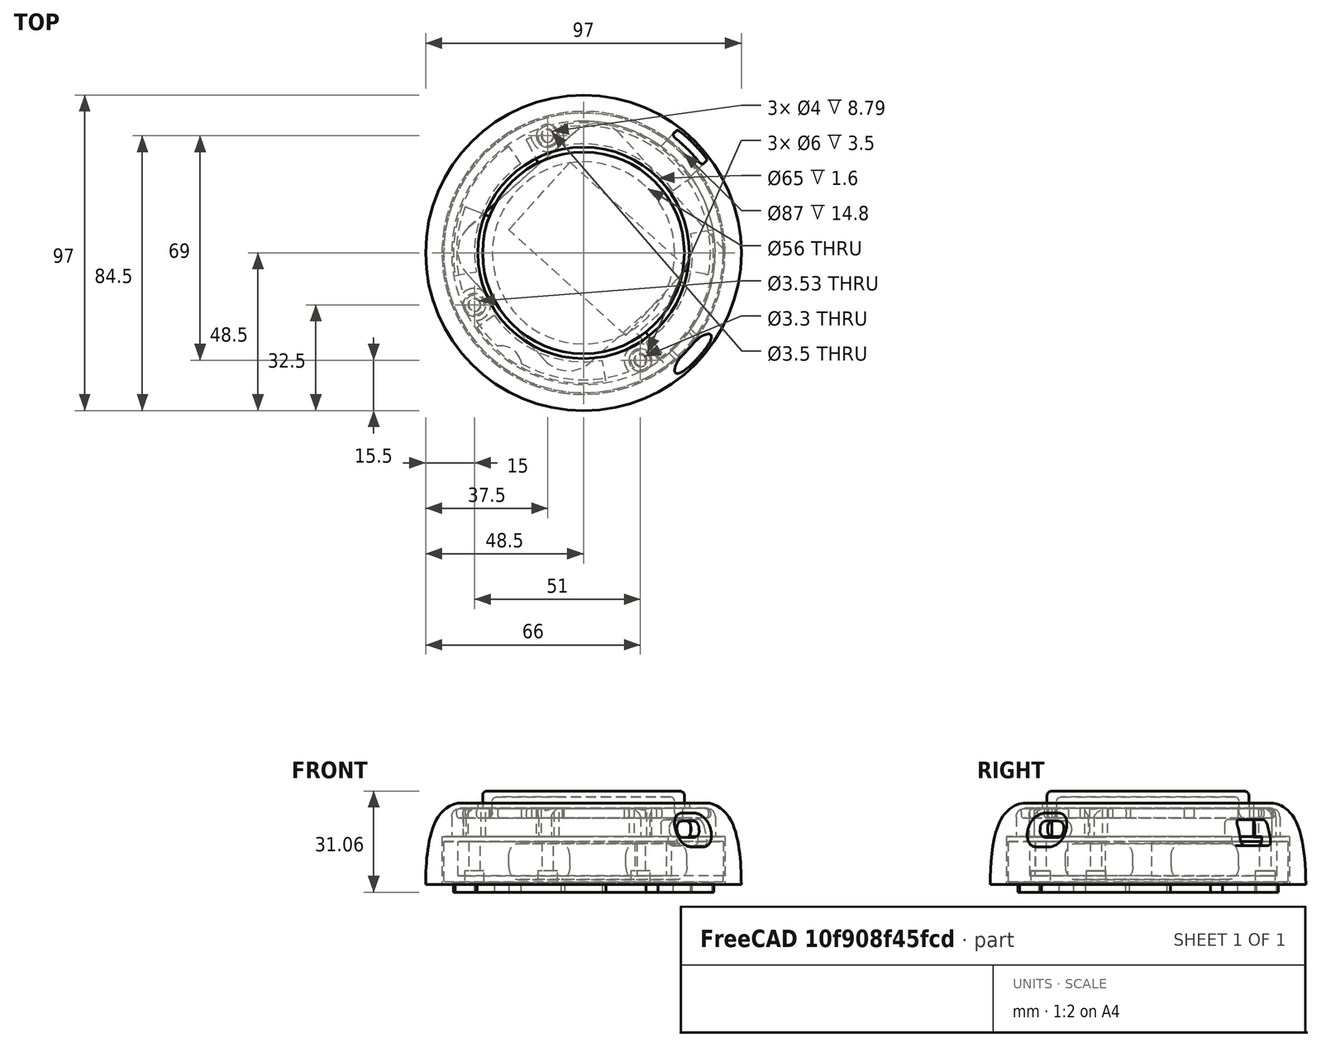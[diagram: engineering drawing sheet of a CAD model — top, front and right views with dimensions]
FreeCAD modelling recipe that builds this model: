
FCSTD DOCUMENT  (FreeCAD 1.0R39109 (Git))
Label: slimCasing_new
License: All rights reserved
LicenseURL: https://en.wikipedia.org/wiki/All_rights_reserved
objects: Sketcher::SketchObject×11, PartDesign::Body×5, PartDesign::Pocket×5, PartDesign::Pad×4, PartDesign::Revolution×2, PartDesign::Plane×2, Mesh::Feature×1, PartDesign::Fillet×1, PartDesign::Chamfer×1, PartDesign::PolarPattern×1
note: 70 computed .brp shape members not serialized (recipe doc carries the construction recipe); baked Part::Feature solids carry a one-line shape summary decoded from their .brp

FEATURE [Sketcher::SketchObject] Sketch
  ArcFitTolerance = 1e-06
  AttachmentSupport = -> [XZ_Plane]
  FullyConstrained = true
  MakeInternals = false
  MapMode = 5
  Placement = pos=(0,0,0) rot=(1,0,0;1.5708rad)
  sketch-geometry (17):
    g0: LineSegment StartX=-31 StartY=12 StartZ=0 EndX=-31 EndY=8 EndZ=0
    g1: LineSegment StartX=-31 StartY=8 StartZ=0 EndX=-38 EndY=8 EndZ=0
    g2: LineSegment StartX=-39 StartY=7 StartZ=0 EndX=-39 EndY=6 EndZ=0
    g3: LineSegment StartX=-38 StartY=5 StartZ=0 EndX=-29.8 EndY=5 EndZ=0
    g4: LineSegment StartX=-28 StartY=6.8 StartZ=0 EndX=-28 EndY=10.2 EndZ=0
    g5: LineSegment StartX=-26.7 StartY=11.5 StartZ=0 EndX=0 EndY=11.5 EndZ=0
    g6: LineSegment StartX=0 StartY=11.5 StartZ=0 EndX=0 EndY=13.3 EndZ=0
    g7: ArcOfCircle CenterX=-29.7 CenterY=12 CenterZ=0 NormalX=0 NormalY=0 NormalZ=1 AngleXU=0 Radius=1.3 StartAngle=1.5708 EndAngle=3.14159
    g8: ArcOfCircle CenterX=-26.7 CenterY=10.2 CenterZ=0 NormalX=0 NormalY=0 NormalZ=1 AngleXU=0 Radius=1.3 StartAngle=1.5708 EndAngle=3.14159
    g9: GeomPoint [constr] X=-28 Y=11.5 Z=0
    g10: GeomPoint [constr] X=-31 Y=8 Z=0
    g11: ArcOfCircle CenterX=-29.8 CenterY=6.8 CenterZ=0 NormalX=0 NormalY=0 NormalZ=1 AngleXU=0 Radius=1.8 StartAngle=4.71239 EndAngle=6.28319
    g12: GeomPoint [constr] X=-28 Y=5 Z=0
    g13: ArcOfCircle CenterX=-38 CenterY=7 CenterZ=0 NormalX=0 NormalY=0 NormalZ=1 AngleXU=0 Radius=1 StartAngle=1.5708 EndAngle=3.14159
    g14: GeomPoint [constr] X=-39 Y=8 Z=0
    g15: ArcOfCircle CenterX=-38 CenterY=6 CenterZ=0 NormalX=0 NormalY=0 NormalZ=1 AngleXU=0 Radius=1 StartAngle=3.14159 EndAngle=4.71239
    g16: LineSegment StartX=-29.7 StartY=13.3 StartZ=0 EndX=0 EndY=13.3 EndZ=0
  constraints (42):
    c: Vertical(g0)
    c: Horizontal(g1)
    c: Vertical(g2)
    c: Horizontal(g3)
    c: Vertical(g4)
    c: Horizontal(g5)
    c: Coincident(g5,g6)
    c: Vertical(g6)
    c: DistanceY(g10,g9) = 3.5
    c: DistanceX(g10,g9) = 3
    c: DistanceY(g-1,g5) = 11.5
    c: Tangent(g0,g7) = -1.5708
    c: PointOnObject(g9,g4)
    c: PointOnObject(g9,g5)
    c: Tangent(g4,g8) = 1.5708
    c: Tangent(g5,g8) = 1.5708
    c: PointOnObject(g12,g3)
    c: PointOnObject(g12,g4)
    c: Tangent(g3,g11) = -1.5708
    c: Tangent(g4,g11) = -1.5708
    c: PointOnObject(g14,g2)
    c: PointOnObject(g14,g1)
    c: Tangent(g2,g13) = -1.5708
    c: Tangent(g1,g13) = -1.5708
    c: Tangent(g2,g15) = -1.5708
    c: Tangent(g3,g15) = -1.5708
    c: Equal(g7,g8)
    c: Coincident(g1,g10)
    c: Coincident(g0,g1)
    c: DistanceY(g0,g0) = 4
    c: Radius(g11) = 1.8
    c: Equal(g13,g15)
    c: Radius(g13) = 1
    c: PointOnObject(g5,g-2)
    c: DistanceY(g3,g1) = 3
    c: DistanceY(g7,g7) = 1.3
    c: Horizontal(g16)
    c: Coincident(g6,g16)
    c: Tangent(g7,g16) = 1.5708
    c: Distance(g0,g-2) = 31
    c: Distance(g9,g16) = 1.8
    c: Distance(g2,g-2) = 39
FEATURE [Mesh::Feature] PCB_Board  label="PCB Board"
  Placement = pos=(-64.6,63.9,0.05) rot=(0,0,1;0rad)
FEATURE [PartDesign::Revolution] Revolution
  Angle = 360
  Angle2 = 60
  Axis = (0,2e-16,1)
  Base = (0,0,0)
  Placement = pos=(0,0,0) rot=(1,0,0;1.5708rad)
  Profile = -> Sketch
  ReferenceAxis = -> Sketch [V_Axis]
  Refine = true
  Suppressed = false
  Type = 0
FEATURE [Sketcher::SketchObject] Sketch001
  ArcFitTolerance = 1e-06
  AttachmentSupport = -> [Revolution]
  FullyConstrained = false
  MakeInternals = false
  MapMode = 5
  Placement = pos=(0,2.2e-15,5) rot=(1,0,0;3.14159rad)
  sketch-geometry (17):
    g0: ArcOfCircle CenterX=25.2748 CenterY=34.7877 CenterZ=0 NormalX=0 NormalY=0 NormalZ=1 AngleXU=0 Radius=6.2 StartAngle=2.58543 EndAngle=5.58271
    g1: ArcOfCircle CenterX=0 CenterY=0 CenterZ=0 NormalX=0 NormalY=0 NormalZ=1 AngleXU=0 Radius=43 StartAngle=0.798167 EndAngle=1.08679
    g2: LineSegment [constr] StartX=25.2748 StartY=34.7877 StartZ=0 EndX=0 EndY=0 EndZ=0
    g3: ArcOfCircle CenterX=0 CenterY=0 CenterZ=0 NormalX=0 NormalY=0 NormalZ=1 AngleXU=0 Radius=43 StartAngle=2.2555 EndAngle=2.98853
    g4: LineSegment [constr] StartX=0 StartY=0 StartZ=0 EndX=-42.4024 EndY=26.496 EndZ=0
    g5: LineSegment [constr] StartX=0 StartY=0 StartZ=0 EndX=32.3963 EndY=-28.2751 EndZ=0
    g6: LineSegment StartX=40.3774 StartY=-14.7873 StartZ=0 EndX=29.1093 EndY=-10.6606 EndZ=0
    g7: LineSegment StartX=20.1117 StartY=-38.0069 StartZ=0 EndX=14.4991 EndY=-27.4003 EndZ=0
    g8: ArcOfCircle CenterX=0 CenterY=0 CenterZ=0 NormalX=0 NormalY=0 NormalZ=1 AngleXU=0 Radius=31 StartAngle=5.19909 EndAngle=5.93213
    g9: ArcOfCircle CenterX=0 CenterY=0 CenterZ=0 NormalX=0 NormalY=0 NormalZ=1 AngleXU=0 Radius=43 StartAngle=5.19909 EndAngle=5.93213
    g10: LineSegment [constr] StartX=14.4991 StartY=-27.4003 StartZ=0 EndX=29.1093 EndY=-10.6606 EndZ=0
    g11: Circle CenterX=-37.7489 CenterY=-0.6901 CenterZ=0 NormalX=0 NormalY=0 NormalZ=1 AngleXU=0 Radius=5
    g12: Circle CenterX=4.78434 CenterY=36.8193 CenterZ=0 NormalX=0 NormalY=0 NormalZ=1 AngleXU=0 Radius=5
    g13: Circle CenterX=36.7704 CenterY=-6.49344 CenterZ=0 NormalX=0 NormalY=0 NormalZ=1 AngleXU=0 Radius=5
    g14: ArcOfCircle CenterX=0 CenterY=0 CenterZ=0 NormalX=0 NormalY=0 NormalZ=1 AngleXU=0 Radius=31 StartAngle=2.2555 EndAngle=2.98853
    g15: LineSegment StartX=-19.6056 StartY=24.0129 StartZ=0 EndX=-27.1949 EndY=33.3082 EndZ=0
    g16: LineSegment StartX=-42.4973 StartY=6.55585 StartZ=0 EndX=-30.6376 EndY=4.72631 EndZ=0
  constraints (48):
    c: Coincident(g1,g0)
    c: Coincident(g1,g0)
    c: Coincident(g2,g0)
    c: Angle(g-1,g2) = 0.942478
    c: Distance(g4,g4) = 50
    c: Angle(g4,g-1) = 0.558505
    c: Coincident(g8,g6)
    c: Coincident(g8,g7)
    c: Distance(g6,g6) = 12
    c: Coincident(g9,g6)
    c: Coincident(g9,g7)
    c: Coincident(g10,g7)
    c: Coincident(g10,g6)
    c: Perpendicular(g5,g10)
    c: Equal(g13,g12)
    c: Equal(g11,g12)
    c: Diameter(g12) = 10
    c: DistanceX(g11,g1) = 37.7489
    c: DistanceY(g11,g1) = 0.6901
    c: DistanceX(g13) = 36.7704
    c: DistanceY(g13) = -6.49344
    c: DistanceX(g12) = 4.78434
    c: DistanceY(g12) = 36.8193
    c: Coincident(g1,g2)
    c: Coincident(g1,g3)
    c: Coincident(g1,g4)
    c: Coincident(g1,g5)
    c: Coincident(g1,g8)
    c: Coincident(g1,g9)
    c: Coincident(g1,g-1)
    c: Radius(g0) = 6.2
    c: Distance(g0,g1) = 43
    c: PointOnObject(g0,g1)
    c: Radius(g3) = 43
    c: Radius(g9) = 43
    c: Angle(g7,g6) = 0.733038
    c: PointOnObject(g5,g9)
    c: Coincident(g14,g1)
    c: Equal(g8,g14)
    c: Coincident(g15,g14)
    c: Coincident(g15,g3)
    c: Coincident(g16,g3)
    c: Coincident(g16,g14)
    c: Perpendicular(g14,g16)
    c: Perpendicular(g14,g15)
    c: Angle(g15,g16) = 0.733038
    c: Distance(g16,g16) = 12
    c: Perpendicular(g9,g7)
FEATURE [Sketcher::SketchObject] Sketch027
  ArcFitTolerance = 0
  FullyConstrained = true
  MakeInternals = false
  MapMode = 5
  sketch-geometry (4):
    g0: LineSegment StartX=-24.25 StartY=14 StartZ=0 EndX=24.25 EndY=14 EndZ=0
    g1: LineSegment StartX=24.25 StartY=14 StartZ=0 EndX=24.25 EndY=-14 EndZ=0
    g2: LineSegment StartX=24.25 StartY=-14 StartZ=0 EndX=-24.25 EndY=-14 EndZ=0
    g3: LineSegment StartX=-24.25 StartY=-14 StartZ=0 EndX=-24.25 EndY=14 EndZ=0
  constraints (11):
    c: Coincident(g0,g1)
    c: Coincident(g1,g2)
    c: Coincident(g2,g3)
    c: Coincident(g3,g0)
    c: Horizontal(g0)
    c: Horizontal(g2)
    c: Vertical(g1)
    c: Vertical(g3)
    c: Symmetric(g0,g1,g-1)
    c: DistanceX(g0,g0) = 48.5
    c: DistanceY(g1,g1) = 28
FEATURE [PartDesign::Pad] Pad004
  Direction = (0,0,1)
  Length = 11
  Length2 = 10
  Profile = -> Sketch027
  ReferenceAxis = -> Sketch027 [N_Axis]
  Suppressed = false
  Type = 0
FEATURE [PartDesign::Fillet] Fillet002
  Base = -> Pad004 [Edge4,Edge3,Edge10,Edge9]
  BaseFeature = -> Pad004
  Radius = 4
  SupportTransform = false
  Suppressed = false
  UseAllEdges = false
FEATURE [PartDesign::Body] Body005  label="Batterie"
  AllowCompound = false
  Group = -> [Sketch027,Pad004,Fillet002]
  Placement = pos=(4.42123,1.23614,-11.6) rot=(0,0,1;5.5484rad)
  Tip = -> Fillet002
FEATURE [PartDesign::Pocket] Pocket
  BaseFeature = -> Revolution
  Direction = (0,0,1)
  Length = 5
  Length2 = 5
  Placement = pos=(0,0,0) rot=(1,0,0;1.5708rad)
  Profile = -> Sketch001
  ReferenceAxis = -> Sketch001 [N_Axis]
  Refine = true
  Suppressed = false
  Type = 0
FEATURE [PartDesign::Body] Body  label="Buzzerkopf"
  AllowCompound = false
  Group = -> [Sketch,Revolution,Sketch001,Pocket]
  Origin = -> Origin
  Placement = pos=(0,0,2.23) rot=(0,0,1;5.02655rad)
  Tip = -> Pocket
FEATURE [Sketcher::SketchObject] Sketch028
  ArcFitTolerance = 1e-06
  AttachmentSupport = -> [YZ_Plane001]
  FullyConstrained = false
  MakeInternals = false
  MapMode = 5
  Placement = pos=(0,0,0) rot=(0.57735,0.57735,0.57735;2.0944rad)
  sketch-geometry (16):
    g0: LineSegment StartX=32.5 StartY=10.29 StartZ=0 EndX=37.81 EndY=10.29 EndZ=0
    g1: LineSegment StartX=40.5 StartY=7.6 StartZ=0 EndX=40.5 EndY=1.6 EndZ=0
    g2: LineSegment StartX=40.5 StartY=1.6 StartZ=0 EndX=43.5 EndY=1.6 EndZ=0
    g3: LineSegment StartX=43.5 StartY=1.6 StartZ=0 EndX=43.5 EndY=-13.2 EndZ=0
    g4: LineSegment StartX=43.5 StartY=-13.2 StartZ=0 EndX=48.5 EndY=-13.2 EndZ=0
    g5-g8: Circle [constr] x4 (B-spline internal-alignment scaffolding for g9; pole/knot coordinates omitted)
    g9: BSplineCurve PolesCount=5 KnotsCount=3 Degree=3 IsPeriodic=0
    g10: GeomPoint [constr] X=37.5 Y=11.89 Z=0
    g11: GeomPoint [constr] X=48.5 Y=-13.2 Z=0
    g12: ArcOfCircle CenterX=37.81 CenterY=7.6 CenterZ=0 NormalX=0 NormalY=0 NormalZ=1 AngleXU=0 Radius=2.69 StartAngle=0 EndAngle=1.5708
    g13: GeomPoint [constr] X=40.5 Y=10.29 Z=0
    g14: LineSegment StartX=37.5 StartY=11.89 StartZ=0 EndX=32.5 EndY=11.89 EndZ=0
    g15: LineSegment StartX=32.5 StartY=11.89 StartZ=0 EndX=32.5 EndY=10.29 EndZ=0
  constraints (41):
    c: Horizontal(g0)
    c: Coincident(g1,g2)
    c: Horizontal(g2)
    c: Coincident(g2,g3)
    c: Vertical(g3)
    c: Coincident(g3,g4)
    c: Horizontal(g4)
    c: InternalAlignment(g5-g8 -> g9) x4
    c: InternalAlignment(g10,g9)
    c: InternalAlignment(g11,g9)
    c: Coincident(g8,g4)
    c: Vertical(g1)
    c: DistanceX(g4,g4) = 5
    c: Distance(g2,g2) = 3
    c: Distance(g0,g-2) = 32.5
    c: Horizontal(g5,g9)
    c: Vertical(g7,g9)
    c: PointOnObject(g13,g0)
    c: PointOnObject(g13,g1)
    c: Tangent(g0,g12) = 1.5708
    c: Tangent(g1,g12) = 1.5708
    c: DistanceY(g1,g1) = 6
    c: Radius(g12) = 2.69
    c: DistanceY(g3,g3) = 14.8
    c: DistanceX(g5,g6) = 8
    c: DistanceY(g6,g5) = 1.8
    c: DistanceY(g9,g7) = 6.93
    c: Distance(g2,g-1) = 1.6
    c: Distance(g5,g-2) = 39
    c: Distance(g13,g-2) = 40.5
    c: Coincident(g14,g9)
    c: Horizontal(g14)
    c: Coincident(g15,g14)
    c: Coincident(g15,g0)
    c: Vertical(g15)
    c: DistanceY(g15,g15) = 1.6
    c: DistanceX(g14,g14) = 5
    c: Weight(g5) = 2.75
    c: Weight(g6) = 2.71
    c: Weight(g7) = 2.65
    c: Weight(g8) = 2.04
FEATURE [PartDesign::Revolution] Revolution001
  Angle = 360
  Angle2 = 60
  Axis = (0,0,1)
  Base = (0,0,0)
  Placement = pos=(0,0,0) rot=(1,1,1;2.0944rad)
  Profile = -> Sketch028
  ReferenceAxis = -> Sketch028 [V_Axis]
  Refine = true
  Reversed = true
  Suppressed = false
  Type = 0
FEATURE [Sketcher::SketchObject] Sketch029
  ArcFitTolerance = 1e-06
  AttachmentOffset = pos=(0,0,1.5) rot=(0,0,1;0rad)
  AttachmentSupport = -> [XY_Plane001]
  FullyConstrained = true
  MakeInternals = false
  MapMode = 5
  Placement = pos=(0,0,1.5) rot=(0,0,1;0rad)
  sketch-geometry (6):
    g0: Circle CenterX=-11 CenterY=36 CenterZ=0 NormalX=0 NormalY=0 NormalZ=1 AngleXU=0 Radius=3.5
    g1: Circle CenterX=17.5 CenterY=-33 CenterZ=0 NormalX=0 NormalY=0 NormalZ=1 AngleXU=0 Radius=3.5
    g2: Circle CenterX=-33.5 CenterY=-16 CenterZ=0 NormalX=0 NormalY=0 NormalZ=1 AngleXU=0 Radius=3.5
    g3: Circle CenterX=-11 CenterY=36 CenterZ=0 NormalX=0 NormalY=0 NormalZ=1 AngleXU=0 Radius=2
    g4: Circle CenterX=-33.5 CenterY=-16 CenterZ=0 NormalX=0 NormalY=0 NormalZ=1 AngleXU=0 Radius=2
    g5: Circle CenterX=17.5 CenterY=-33 CenterZ=0 NormalX=0 NormalY=0 NormalZ=1 AngleXU=0 Radius=2
  constraints (15):
    c: DistanceX(g0) = -11
    c: DistanceY(g0) = 36
    c: DistanceX(g2) = -33.5
    c: DistanceY(g2) = -16
    c: DistanceX(g1) = 17.5
    c: DistanceY(g1) = -33
    c: Equal(g1,g2)
    c: Equal(g2,g0)
    c: Diameter(g0) = 7
    c: Coincident(g3,g0)
    c: Coincident(g4,g2)
    c: Coincident(g5,g1)
    c: Equal(g5,g4)
    c: Equal(g4,g3)
    c: Diameter(g3) = 4
FEATURE [PartDesign::Pad] Pad
  BaseFeature = -> Revolution001
  Direction = (0,0,1)
  Length = 9
  Length2 = 10
  Placement = pos=(0,0,0) rot=(1,1,1;2.0944rad)
  Profile = -> Sketch029
  ReferenceAxis = -> Sketch029 [N_Axis]
  Refine = true
  Suppressed = false
  Type = 0
FEATURE [Sketcher::SketchObject] Sketch030
  ArcFitTolerance = 1e-06
  AttachmentSupport = -> [XY_Plane002]
  FullyConstrained = true
  MakeInternals = false
  MapMode = 5
  sketch-geometry (4):
    g0: Circle CenterX=0 CenterY=0 CenterZ=0 NormalX=0 NormalY=0 NormalZ=1 AngleXU=0 Radius=43
    g1: Circle CenterX=-33.5 CenterY=-16 CenterZ=0 NormalX=0 NormalY=0 NormalZ=1 AngleXU=0 Radius=1.765
    g2: Circle CenterX=17.5 CenterY=-33 CenterZ=0 NormalX=0 NormalY=0 NormalZ=1 AngleXU=0 Radius=1.65
    g3: Circle CenterX=-11 CenterY=36 CenterZ=0 NormalX=0 NormalY=0 NormalZ=1 AngleXU=0 Radius=1.75
  constraints (11):
    c: Diameter(g0) = 86
    c: Coincident(g0,g-1)
    c: Diameter(g1) = 3.53
    c: Diameter(g2) = 3.3
    c: Diameter(g3) = 3.5
    c: DistanceX(g3) = -11
    c: DistanceY(g3) = 36
    c: DistanceX(g1) = -33.5
    c: DistanceY(g1) = -16
    c: DistanceX(g2) = 17.5
    c: DistanceY(g2) = -33
FEATURE [PartDesign::Pad] Pad005
  Direction = (0,0,1)
  Length = 12.5
  Length2 = 10
  Profile = -> Sketch030
  ReferenceAxis = -> Sketch030 [N_Axis]
  Refine = true
  Suppressed = false
  Type = 0
FEATURE [Sketcher::SketchObject] Sketch031
  ArcFitTolerance = 1e-06
  AttachmentSupport = -> [Pad005]
  ExternalGeometry = -> [Pad005]
  FullyConstrained = true
  MakeInternals = false
  MapMode = 5
  Placement = pos=(0,0,12.5) rot=(0,0,1;0rad)
  sketch-geometry (17):
    g0: LineSegment StartX=11.2969 StartY=36.4811 StartZ=0 EndX=53.7611 EndY=-10.9052 EndZ=0
    g1: LineSegment StartX=53.7611 StartY=-10.9052 StartZ=0 EndX=26.2063 EndY=-35.5979 EndZ=0
    g2: LineSegment StartX=26.2063 StartY=-35.5979 StartZ=0 EndX=16.4633 EndY=-24.7257 EndZ=0
    g3: LineSegment StartX=16.4633 StartY=-24.7257 StartZ=0 EndX=26.6186 EndY=-15.6253 EndZ=0
    g4: LineSegment StartX=24.6164 StartY=-13.3911 StartZ=0 EndX=1.9023 EndY=-33.7459 EndZ=0
    g5: LineSegment StartX=-11.8966 StartY=-32.9899 StartZ=0 EndX=-36.0943 EndY=-5.98746 EndZ=0
    g6: LineSegment StartX=-35.3384 StartY=7.81147 StartZ=0 EndX=-2.50207 EndY=37.2371 EndZ=0
    g7: ArcOfCircle CenterX=25.6175 CenterY=-14.5082 CenterZ=0 NormalX=0 NormalY=0 NormalZ=1 AngleXU=0 Radius=1.5 StartAngle=5.44306 EndAngle=8.58465
    g8: Circle [constr] CenterX=-11 CenterY=36 CenterZ=0 NormalX=0 NormalY=0 NormalZ=1 AngleXU=0 Radius=4.75
    g9: Circle [constr] CenterX=-33.5 CenterY=-16 CenterZ=0 NormalX=0 NormalY=0 NormalZ=1 AngleXU=0 Radius=4.75
    g10: Circle [constr] CenterX=17.5 CenterY=-33 CenterZ=0 NormalX=0 NormalY=0 NormalZ=1 AngleXU=0 Radius=4.75
    g11: ArcOfCircle CenterX=-28.8169 CenterY=0.534046 CenterZ=0 NormalX=0 NormalY=0 NormalZ=1 AngleXU=0 Radius=9.77195 StartAngle=2.30147 EndAngle=3.87226
    g12: GeomPoint [constr] X=-42.6158 Y=1.28997 Z=0
    g13: ArcOfCircle CenterX=4.01944 CenterY=29.9596 CenterZ=0 NormalX=0 NormalY=0 NormalZ=1 AngleXU=0 Radius=9.77195 StartAngle=0.730672 EndAngle=2.30147
    g14: GeomPoint [constr] X=4.77536 Y=43.7586 Z=0
    g15: ArcOfCircle CenterX=-4.61921 CenterY=-26.4684 CenterZ=0 NormalX=0 NormalY=0 NormalZ=1 AngleXU=0 Radius=9.77195 StartAngle=3.87226 EndAngle=5.44306
    g16: GeomPoint [constr] X=-5.37513 Y=-40.2674 Z=0
  constraints (43):
    c: Coincident(g0,g1)
    c: Coincident(g1,g2)
    c: Coincident(g2,g3)
    c: Perpendicular(g6,g5)
    c: Perpendicular(g0,g6)
    c: Perpendicular(g1,g2)
    c: Perpendicular(g1,g0)
    c: Distance(g1,g1) = 37
    c: Tangent(g7,g3) = -1.5708
    c: Tangent(g7,g4) = -1.5708
    c: Perpendicular(g3,g2)
    c: Perpendicular(g5,g4)
    c: Distance(g4,g3) = 3
    c: Coincident(g8,g-5)
    c: Coincident(g9,g-3)
    c: Coincident(g10,g-4)
    c: Equal(g10,g9)
    c: Equal(g9,g8)
    c: Distance(g-5,g8) = 3
    c: Tangent(g2,g10)
    c: Tangent(g9,g5)
    c: Tangent(g6,g8)
    c: PointOnObject(g12,g5)
    c: PointOnObject(g12,g6)
    c: Tangent(g5,g11) = 1.5708
    c: Tangent(g6,g11) = 1.5708
    c: PointOnObject(g14,g6)
    c: PointOnObject(g14,g0)
    c: Tangent(g6,g13) = 1.5708
    c: Tangent(g0,g13) = 1.5708
    c: PointOnObject(g16,g4)
    c: PointOnObject(g16,g5)
    c: Tangent(g4,g15) = 1.5708
    c: Tangent(g5,g15) = 1.5708
    c: Equal(g13,g11)
    c: Equal(g11,g15)
    c: Distance(g13,g-6) = 3
    c: Distance(g11,g-6) = 4.40619
    c: Distance(g15,g-6) = 6.35956
    c: Distance(g4,g4) = 30.5
    c: DistanceX(g7) = 25.6175
    c: DistanceY(g7) = -14.5082
    c: Distance(g-6,g1) = 1
FEATURE [PartDesign::Pocket] Pocket001
  BaseFeature = -> Pad005
  Direction = (0,0,-1)
  Length = 5
  Length2 = 5
  Offset = -2
  Profile = -> Sketch031
  ReferenceAxis = -> Sketch031 [N_Axis]
  Refine = true
  Suppressed = false
  Type = 2
FEATURE [Sketcher::SketchObject] Sketch032
  ArcFitTolerance = 1e-06
  AttachmentSupport = -> [XY_Plane002]
  FullyConstrained = true
  MakeInternals = false
  MapMode = 5
  sketch-geometry (3):
    g0: Circle CenterX=-33.5 CenterY=-16 CenterZ=0 NormalX=0 NormalY=0 NormalZ=1 AngleXU=0 Radius=3
    g1: Circle CenterX=17.5 CenterY=-33 CenterZ=0 NormalX=0 NormalY=0 NormalZ=1 AngleXU=0 Radius=3
    g2: Circle CenterX=-11 CenterY=36 CenterZ=0 NormalX=0 NormalY=0 NormalZ=1 AngleXU=0 Radius=3
  constraints (9):
    c: DistanceX(g2) = -11
    c: DistanceY(g2) = 36
    c: DistanceX(g0) = -33.5
    c: DistanceY(g0) = -16
    c: DistanceX(g1) = 17.5
    c: DistanceY(g1) = -33
    c: Equal(g0,g1)
    c: Equal(g1,g2)
    c: Diameter(g2) = 6
FEATURE [PartDesign::Pocket] Pocket002
  BaseFeature = -> Pocket001
  Direction = (0,0,-1)
  Length = 3.5
  Length2 = 5
  Profile = -> Sketch032
  ReferenceAxis = -> Sketch032 [N_Axis]
  Refine = true
  Reversed = true
  Suppressed = false
  Type = 0
FEATURE [PartDesign::Body] Body007  label="Unterteil"
  AllowCompound = false
  Group = -> [Sketch030,Pad005,Sketch031,Pocket001,Sketch032,Pocket002]
  Origin = -> Origin002
  Placement = pos=(0,0,-12.46) rot=(0,0,1;0rad)
  Tip = -> Pocket002
FEATURE [PartDesign::Plane] DatumPlane
  AttachmentOffset = pos=(0,69,0) rot=(-1,0,0;0.785398rad)
  AttachmentSupport = -> [Pad]
  Length = 66.5625
  MapMode = 4
  Placement = pos=(69,0,0) rot=(0.678598,0.281085,0.678598;3.68962rad)
  ResizeMode = 0
  Width = 153.721
FEATURE [Sketcher::SketchObject] Sketch033
  ArcFitTolerance = 1e-06
  AttachmentSupport = -> [DatumPlane]
  FullyConstrained = true
  MakeInternals = false
  MapMode = 5
  Placement = pos=(69,0,0) rot=(0.678598,0.281085,0.678598;3.68962rad)
  sketch-geometry (10):
    g0: LineSegment StartX=5.3311 StartY=-42.1309 StartZ=0 EndX=0.331099 EndY=-42.1309 EndZ=0
    g1: LineSegment StartX=-1.1689 StartY=-43.6309 StartZ=0 EndX=-1.1689 EndY=-53.6309 EndZ=0
    g2: LineSegment StartX=0.331099 StartY=-55.1309 StartZ=0 EndX=5.3311 EndY=-55.1309 EndZ=0
    g3: LineSegment StartX=6.8311 StartY=-53.6309 StartZ=0 EndX=6.8311 EndY=-43.6309 EndZ=0
    g4: ArcOfCircle CenterX=5.3311 CenterY=-43.6309 CenterZ=0 NormalX=0 NormalY=0 NormalZ=1 AngleXU=0 Radius=1.5 StartAngle=0 EndAngle=1.5708
    g5: ArcOfCircle CenterX=0.331099 CenterY=-43.6309 CenterZ=0 NormalX=0 NormalY=0 NormalZ=1 AngleXU=0 Radius=1.5 StartAngle=1.5708 EndAngle=3.14159
    g6: ArcOfCircle CenterX=0.331099 CenterY=-53.6309 CenterZ=0 NormalX=0 NormalY=0 NormalZ=1 AngleXU=0 Radius=1.5 StartAngle=3.14159 EndAngle=4.71239
    g7: ArcOfCircle CenterX=5.3311 CenterY=-53.6309 CenterZ=0 NormalX=0 NormalY=0 NormalZ=1 AngleXU=0 Radius=1.5 StartAngle=4.71239 EndAngle=6.28319
    g8: GeomPoint [constr] X=6.8311 Y=-42.1309 Z=0
    g9: GeomPoint [constr] X=-1.1689 Y=-55.1309 Z=0
  constraints (24):
    c: Tangent(g0,g4) = -1.5708
    c: Tangent(g0,g5) = -1.5708
    c: Tangent(g1,g5) = -1.5708
    c: Tangent(g1,g6) = -1.5708
    c: Tangent(g2,g6) = -1.5708
    c: Tangent(g2,g7) = -1.5708
    c: Tangent(g3,g7) = -1.5708
    c: Tangent(g3,g4) = -1.5708
    c: Horizontal(g0)
    c: Horizontal(g2)
    c: Vertical(g1)
    c: Vertical(g3)
    c: Equal(g4,g5)
    c: Equal(g5,g6)
    c: Equal(g6,g7)
    c: PointOnObject(g8,g0)
    c: PointOnObject(g8,g3)
    c: PointOnObject(g9,g1)
    c: PointOnObject(g9,g2)
    c: Radius(g4) = 1.5
    c: DistanceY(g2,g0) = 13
    c: DistanceX(g1,g3) = 8
    c: DistanceX(g0) = 5.3311
    c: DistanceY(g0) = -42.1309
FEATURE [PartDesign::Pocket] Pocket003
  BaseFeature = -> Pad
  Direction = (-0.707107,-0.707107,0)
  Length = 11
  Length2 = 5
  Placement = pos=(0,0,0) rot=(1,1,1;2.0944rad)
  Profile = -> Sketch033
  ReferenceAxis = -> Sketch033 [N_Axis]
  Refine = true
  Suppressed = false
  Type = 0
FEATURE [PartDesign::Plane] DatumPlane001
  AttachmentOffset = pos=(-72,0,0) rot=(0,-1,0;0.767945rad)
  AttachmentSupport = -> [Revolution001]
  Length = 153.699
  MapMode = 2
  Placement = pos=(0,-72,0) rot=(0.85738,0.363936,0.363936;1.72407rad)
  ResizeMode = 0
  Width = 66.5613
FEATURE [Sketcher::SketchObject] Sketch034
  ArcFitTolerance = 1e-06
  AttachmentSupport = -> [DatumPlane001]
  FullyConstrained = true
  MakeInternals = false
  MapMode = 5
  Placement = pos=(0,-72,0) rot=(0.85738,0.363936,0.363936;1.72407rad)
  sketch-geometry (10):
    g0: LineSegment StartX=47.8843 StartY=4.03235 StartZ=0 EndX=47.8843 EndY=3.63235 EndZ=0
    g1: LineSegment StartX=50.1843 StartY=1.33235 StartZ=0 EndX=55.5843 EndY=1.33235 EndZ=0
    g2: LineSegment StartX=57.8843 StartY=3.63235 StartZ=0 EndX=57.8843 EndY=4.03235 EndZ=0
    g3: LineSegment StartX=55.5843 StartY=6.33235 StartZ=0 EndX=50.1843 EndY=6.33235 EndZ=0
    g4: ArcOfCircle CenterX=50.1843 CenterY=4.03235 CenterZ=0 NormalX=0 NormalY=0 NormalZ=1 AngleXU=0 Radius=2.3 StartAngle=1.5708 EndAngle=3.14159
    g5: ArcOfCircle CenterX=50.1843 CenterY=3.63235 CenterZ=0 NormalX=0 NormalY=0 NormalZ=1 AngleXU=0 Radius=2.3 StartAngle=3.14159 EndAngle=4.71239
    g6: ArcOfCircle CenterX=55.5843 CenterY=3.63235 CenterZ=0 NormalX=0 NormalY=0 NormalZ=1 AngleXU=0 Radius=2.3 StartAngle=4.71239 EndAngle=6.28319
    g7: ArcOfCircle CenterX=55.5843 CenterY=4.03235 CenterZ=0 NormalX=0 NormalY=0 NormalZ=1 AngleXU=0 Radius=2.3 StartAngle=0 EndAngle=1.5708
    g8: GeomPoint [constr] X=47.8843 Y=6.33235 Z=0
    g9: GeomPoint [constr] X=57.8843 Y=1.33235 Z=0
  constraints (24):
    c: Tangent(g0,g4) = -1.5708
    c: Tangent(g0,g5) = -1.5708
    c: Tangent(g1,g5) = -1.5708
    c: Tangent(g1,g6) = -1.5708
    c: Tangent(g2,g6) = -1.5708
    c: Tangent(g2,g7) = -1.5708
    c: Tangent(g3,g7) = -1.5708
    c: Tangent(g3,g4) = -1.5708
    c: Vertical(g0)
    c: Vertical(g2)
    c: Horizontal(g1)
    c: Horizontal(g3)
    c: Equal(g4,g5)
    c: Equal(g5,g6)
    c: Equal(g6,g7)
    c: PointOnObject(g8,g0)
    c: PointOnObject(g8,g3)
    c: PointOnObject(g9,g1)
    c: PointOnObject(g9,g2)
    c: DistanceX(g0,g2) = 10
    c: DistanceY(g1,g3) = 5
    c: Radius(g7) = 2.3
    c: DistanceX(g3) = 50.1843
    c: DistanceY(g3) = 6.33235
FEATURE [PartDesign::Pocket] Pocket004
  BaseFeature = -> Pocket003
  Direction = (-0.71934,0.694658,0)
  Length = 23
  Length2 = 5
  Placement = pos=(0,0,0) rot=(1,1,1;2.0944rad)
  Profile = -> Sketch034
  ReferenceAxis = -> Sketch034 [N_Axis]
  Refine = true
  Suppressed = false
  Type = 0
FEATURE [PartDesign::Chamfer] Chamfer
  Angle = 45
  Base = -> Pocket004 [Edge20]
  BaseFeature = -> Pocket004
  ChamferType = 2
  FlipDirection = false
  Placement = pos=(0,0,0) rot=(1,1,1;2.0944rad)
  Refine = true
  Size = 3
  Size2 = 1
  SupportTransform = false
  Suppressed = false
  UseAllEdges = false
FEATURE [PartDesign::Body] Body006  label="Aussenhuelle"
  AllowCompound = false
  Group = -> [Sketch028,Revolution001,Sketch029,Pad,DatumPlane,Sketch033,Pocket003,DatumPlane001,Sketch034,Pocket004,Chamfer]
  Origin = -> Origin001
  Tip = -> Chamfer
FEATURE [Sketcher::SketchObject] Sketch035
  ArcFitTolerance = 1e-06
  AttachmentSupport = -> [XY_Plane003]
  FullyConstrained = true
  MakeInternals = false
  MapMode = 5
  sketch-geometry (6):
    g0: ArcOfCircle CenterX=0 CenterY=0 CenterZ=0 NormalX=0 NormalY=0 NormalZ=1 AngleXU=0 Radius=33.5 StartAngle=3.82227 EndAngle=4.95674
    g1: ArcOfCircle CenterX=0 CenterY=0 CenterZ=0 NormalX=0 NormalY=0 NormalZ=1 AngleXU=0 Radius=40 StartAngle=3.82227 EndAngle=4.95674
    g2: LineSegment StartX=9.67688 StartY=-38.8118 StartZ=0 EndX=8.10438 EndY=-32.5049 EndZ=0
    g3: LineSegment StartX=-26.0344 StartY=-21.0822 StartZ=0 EndX=-31.0858 EndY=-25.1728 EndZ=0
    g4: LineSegment [constr] StartX=-26.0344 StartY=-21.0822 StartZ=0 EndX=0 EndY=0 EndZ=0
    g5: LineSegment [constr] StartX=8.10438 StartY=-32.5049 StartZ=0 EndX=0 EndY=0 EndZ=0
  constraints (16):
    c: Coincident(g0,g-1)
    c: Coincident(g1,g0)
    c: Coincident(g2,g1)
    c: Coincident(g2,g0)
    c: Coincident(g3,g0)
    c: Coincident(g3,g1)
    c: Coincident(g4,g0)
    c: Coincident(g4,g0)
    c: Coincident(g5,g0)
    c: Coincident(g5,g0)
    c: Parallel(g5,g2)
    c: Parallel(g3,g4)
    c: Distance(g3,g3) = 6.5
    c: Angle(g4,g5) = 1.13446
    c: Distance(g1,g0) = 40
    c: Angle(g5,g-1) = 1.32645
FEATURE [PartDesign::Pad] Pad006
  Direction = (0,0,1)
  Length = 3
  Length2 = 10
  Profile = -> Sketch035
  ReferenceAxis = -> Sketch035 [N_Axis]
  Refine = true
  Reversed = true
  Suppressed = false
  Type = 0
FEATURE [PartDesign::PolarPattern] PolarPattern
  Angle = 360
  Axis = -> Sketch035 [N_Axis]
  BaseFeature = -> Pad006
  Mode = 0
  Occurrences = 4
  Offset = 120
  Originals = -> [Pad006]
  Refine = true
  Suppressed = false
  TransformMode = 0
FEATURE [PartDesign::Body] Body008  label="Antirutschfuesse"
  AllowCompound = true
  Group = -> [Sketch035,Pad006,PolarPattern]
  Origin = -> Origin003
  Placement = pos=(0,0,-12.53) rot=(0,0,1;6.21337rad)
  Tip = -> PolarPattern
